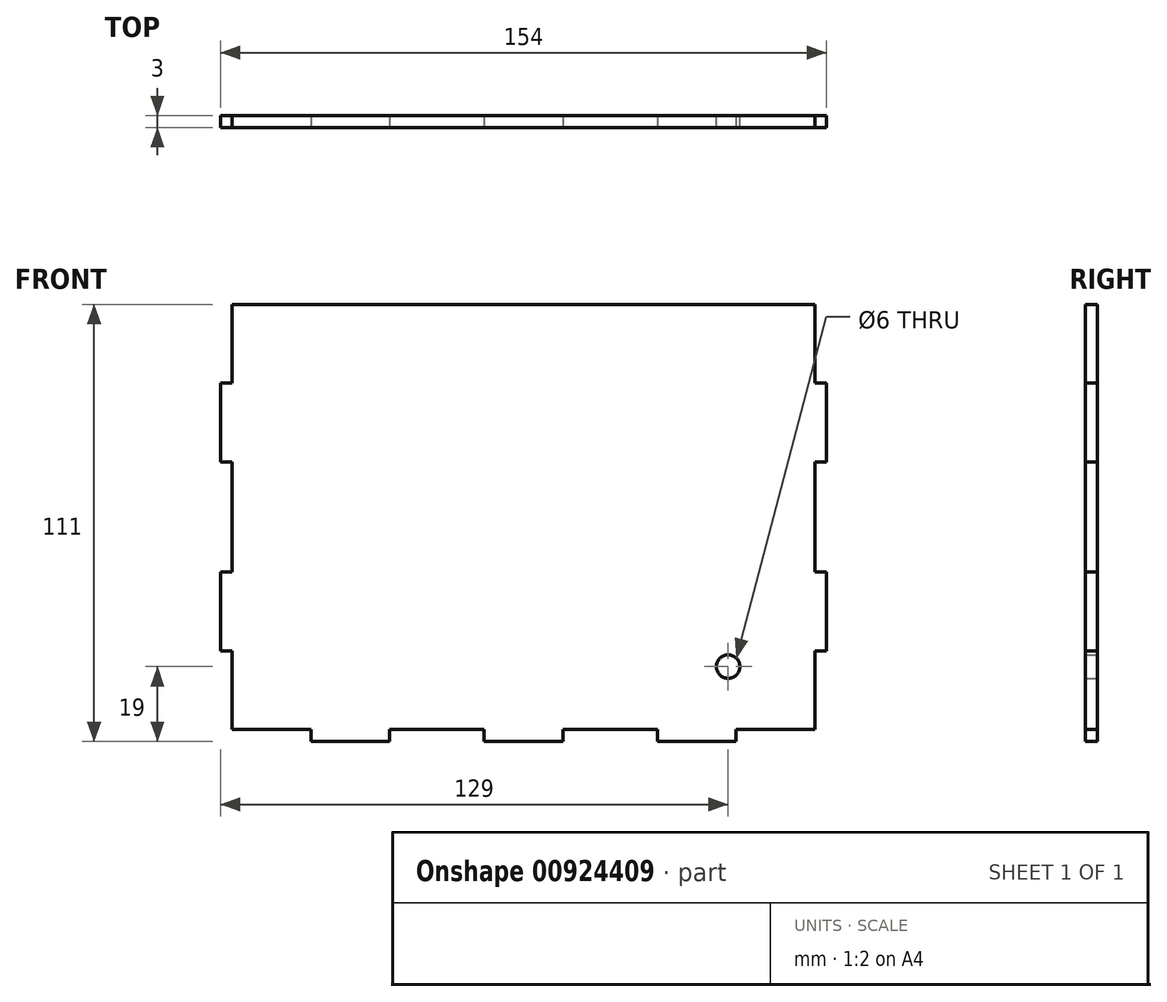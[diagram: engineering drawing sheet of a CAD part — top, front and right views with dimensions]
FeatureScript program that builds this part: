
annotation { "Feature Type Name" : "Feature", "Feature Type Description" : "" }
export const myFeature = defineFeature(function(context is Context, id is Id, definition is map)
    precondition{}
    {
        {
            var Q0;
            Q0=qCreatedBy(makeId("Front.planeOp"),FACE);
            var sketch = newSketch(context, id + "F0", { "sketchPlane" : qUnion([Q0])});
            skLineSegment(sketch, "E0.bottom", {"start": v(3, 0) * mm, "end": v(151, 0) * mm});
            skLineSegment(sketch, "E0.top", {"start": v(0, 111) * mm, "end": v(154, 111) * mm});
            skLineSegment(sketch, "E0.left", {"start": v(0, 3) * mm, "end": v(0, 111) * mm});
            skLineSegment(sketch, "E0.right", {"start": v(154, 3) * mm, "end": v(154, 111) * mm});
            skLineSegment(sketch, "E1", {"start": v(0, 3) * mm, "end": v(3, 3) * mm});
            skLineSegment(sketch, "E2", {"start": v(3, 3) * mm, "end": v(3, 0) * mm});
            skPoint(sketch, "E3", {"position": v(0, 55.5) * mm});
            skPoint(sketch, "E4.orphan", {"position": v(0, 0) * mm});
            skLineSegment(sketch, "E5", {"start": v(154, 3) * mm, "end": v(151, 3) * mm});
            skLineSegment(sketch, "E6", {"start": v(151, 3) * mm, "end": v(151, 0) * mm});
            skSolve(sketch);
        }
        {
            var Q0;
            Q0=qSketchRegion(id+"F0",true);
            extrude(context, id + "F1", {"entities" : qUnion([Q0]), "depth" : 3 * mm, "offsetDistance" : 25 * mm});
        }
        {
            var Q0;
            Q0=makeQuery(id+"F1.opExtrude","CAP_FACE",FACE,{"disambiguationData":[OSD([sQuery(id+"F0.wireOp",EDGE,"E0.bottom"),sQuery(id+"F0.wireOp",EDGE,"E0.top"),sQuery(id+"F0.wireOp",EDGE,"E0.left"),sQuery(id+"F0.wireOp",EDGE,"E0.right"),sQuery(id+"F0.wireOp",EDGE,"RRufsfr7-IhYP-SNug-Ydv5-wJAnrK0FF9g5"),sQuery(id+"F0.wireOp",EDGE,"Sx6Tzd0k-msLp-xlgR-asDp-E0VjmEOWkIfD"),sQuery(id+"F0.wireOp",EDGE,"E1"),sQuery(id+"F0.wireOp",EDGE,"E2"),sQuery(id+"F0.wireOp",EDGE,"xNTWjz4d-b93f-Mlsb-ypie-dKrJAlS9JbEo"),sQuery(id+"F0.wireOp",EDGE,"DDgqVk6M-NDhz-67C2-usiq-S1RQ2gWw5CQe"),sQuery(id+"F0.wireOp",EDGE,"E5"),sQuery(id+"F0.wireOp",EDGE,"E6")])],"isStart":false});
            var sketch = newSketch(context, id + "F2", { "sketchPlane" : qUnion([Q0])});
            skLineSegment(sketch, "E7.bottom", {"start": v(3, 0) * mm, "end": v(23, 0) * mm});
            skLineSegment(sketch, "E7.top", {"start": v(3, 3) * mm, "end": v(23, 3) * mm});
            skLineSegment(sketch, "E7.left", {"start": v(3, 0) * mm, "end": v(3, 3) * mm});
            skLineSegment(sketch, "E7.right", {"start": v(23, 0) * mm, "end": v(23, 3) * mm});
            skLineSegment(sketch, "E8.bottom", {"start": v(43, 0) * mm, "end": v(67, 0) * mm});
            skLineSegment(sketch, "E8.top", {"start": v(43, 3) * mm, "end": v(67, 3) * mm});
            skLineSegment(sketch, "E8.left", {"start": v(43, 0) * mm, "end": v(43, 3) * mm});
            skLineSegment(sketch, "E8.right", {"start": v(67, 0) * mm, "end": v(67, 3) * mm});
            skLineSegment(sketch, "E9.bottom", {"start": v(131, 0) * mm, "end": v(151, 0) * mm});
            skLineSegment(sketch, "E9.top", {"start": v(131, 3) * mm, "end": v(151, 3) * mm});
            skLineSegment(sketch, "E9.left", {"start": v(131, 0) * mm, "end": v(131, 3) * mm});
            skLineSegment(sketch, "E9.right", {"start": v(151, 0) * mm, "end": v(151, 3) * mm});
            skLineSegment(sketch, "E10", {"start": v(23, 1.5) * mm, "end": v(43, 1.5) * mm, "construction": true});
            skLineSegment(sketch, "E11", {"start": v(67, 1.5) * mm, "end": v(87, 1.5) * mm, "construction": true});
            skLineSegment(sketch, "E12.bottom", {"start": v(87, 0) * mm, "end": v(111, 0) * mm});
            skLineSegment(sketch, "E12.top", {"start": v(87, 3) * mm, "end": v(111, 3) * mm});
            skLineSegment(sketch, "E12.left", {"start": v(87, 0) * mm, "end": v(87, 3) * mm});
            skLineSegment(sketch, "E12.right", {"start": v(111, 0) * mm, "end": v(111, 3) * mm});
            skLineSegment(sketch, "E13", {"start": v(111, 1.5) * mm, "end": v(131, 1.5) * mm, "construction": true});
            skSolve(sketch);
        }
        {
            var Q0;
            Q0 = qSketchRegion(id + "F2", true);
            extrude(context, id + "F3", {"entities" : qUnion([Q0]), "operationType" : NewBodyOperationType.REMOVE, "endBound" : BoundingType.THROUGH_ALL, "oppositeDirection" : true, "depth" : 25 * mm, "offsetDistance" : 25 * mm});
        }
        {
            var Q0;
            Q0=makeQuery(id+"F1.opExtrude","CAP_FACE",FACE,{"disambiguationData":[OSD([sQuery(id+"F0.wireOp",EDGE,"E0.bottom"),sQuery(id+"F0.wireOp",EDGE,"E0.top"),sQuery(id+"F0.wireOp",EDGE,"E0.left"),sQuery(id+"F0.wireOp",EDGE,"E0.right"),sQuery(id+"F0.wireOp",EDGE,"E1"),sQuery(id+"F0.wireOp",EDGE,"E2"),sQuery(id+"F0.wireOp",EDGE,"E5"),sQuery(id+"F0.wireOp",EDGE,"E6")])],"isStart":true});
            var sketch = newSketch(context, id + "F4", { "sketchPlane" : qUnion([Q0])});
            skLineSegment(sketch, "E14.bottom", {"start": v(-154, 3) * mm, "end": v(-151, 3) * mm});
            skLineSegment(sketch, "E14.top", {"start": v(-154, 23) * mm, "end": v(-151, 23) * mm});
            skLineSegment(sketch, "E14.left", {"start": v(-154, 3) * mm, "end": v(-154, 23) * mm});
            skLineSegment(sketch, "E14.right", {"start": v(-151, 3) * mm, "end": v(-151, 23) * mm});
            skLineSegment(sketch, "E15.bottom", {"start": v(-154, 43) * mm, "end": v(-151, 43) * mm});
            skLineSegment(sketch, "E15.top", {"start": v(-154, 71) * mm, "end": v(-151, 71) * mm});
            skLineSegment(sketch, "E15.left", {"start": v(-154, 43) * mm, "end": v(-154, 71) * mm});
            skLineSegment(sketch, "E15.right", {"start": v(-151, 43) * mm, "end": v(-151, 71) * mm});
            skLineSegment(sketch, "E16.bottom", {"start": v(-154, 91) * mm, "end": v(-151, 91) * mm});
            skLineSegment(sketch, "E16.top", {"start": v(-154, 111) * mm, "end": v(-151, 111) * mm});
            skLineSegment(sketch, "E16.left", {"start": v(-154, 91) * mm, "end": v(-154, 111) * mm});
            skLineSegment(sketch, "E16.right", {"start": v(-151, 91) * mm, "end": v(-151, 111) * mm});
            skLineSegment(sketch, "E17", {"start": v(-77, 0) * mm, "end": v(-77, 111) * mm, "construction": true});
            skLineSegment(sketch, "E18.MirrorCS", {"start": v(0, 43) * mm, "end": v(-3, 43) * mm});
            skLineSegment(sketch, "E19.MirrorCS", {"start": v(0, 71) * mm, "end": v(-3, 71) * mm});
            skLineSegment(sketch, "E20.MirrorCS", {"start": v(0, 23) * mm, "end": v(-3, 23) * mm});
            skLineSegment(sketch, "E21.MirrorCS", {"start": v(0, 111) * mm, "end": v(-3, 111) * mm});
            skLineSegment(sketch, "E22.MirrorCS", {"start": v(0, 91) * mm, "end": v(-3, 91) * mm});
            skLineSegment(sketch, "E23.MirrorCS", {"start": v(0, 3) * mm, "end": v(-3, 3) * mm});
            skLineSegment(sketch, "E24.MirrorCS", {"start": v(-3, 3) * mm, "end": v(-3, 23) * mm});
            skLineSegment(sketch, "E25.MirrorCS", {"start": v(0, 43) * mm, "end": v(0, 71) * mm});
            skLineSegment(sketch, "E26.MirrorCS", {"start": v(-3, 43) * mm, "end": v(-3, 71) * mm});
            skLineSegment(sketch, "E27.MirrorCS", {"start": v(-3, 91) * mm, "end": v(-3, 111) * mm});
            skLineSegment(sketch, "E28.MirrorCS", {"start": v(0, 3) * mm, "end": v(0, 23) * mm});
            skLineSegment(sketch, "E29.MirrorCS", {"start": v(0, 91) * mm, "end": v(0, 111) * mm});
            skSolve(sketch);
        }
        {
            var Q0;
            Q0 = qSketchRegion(id + "F4", true);
            extrude(context, id + "F5", {"entities" : qUnion([Q0]), "operationType" : NewBodyOperationType.REMOVE, "endBound" : BoundingType.THROUGH_ALL, "oppositeDirection" : true, "depth" : 25 * mm, "offsetDistance" : 25 * mm});
        }
        {
            var Q0;
            Q0=makeQuery(id+"F1.opExtrude","CAP_FACE",FACE,{"disambiguationData":[OSD([sQuery(id+"F0.wireOp",EDGE,"E0.bottom"),sQuery(id+"F0.wireOp",EDGE,"E0.top"),sQuery(id+"F0.wireOp",EDGE,"E0.left"),sQuery(id+"F0.wireOp",EDGE,"E0.right"),sQuery(id+"F0.wireOp",EDGE,"E1"),sQuery(id+"F0.wireOp",EDGE,"E2"),sQuery(id+"F0.wireOp",EDGE,"E5"),sQuery(id+"F0.wireOp",EDGE,"E6")])],"isStart":true});
            var sketch = newSketch(context, id + "F6", { "sketchPlane" : qUnion([Q0])});
            skCircle(sketch, "E30", {"center": v(-129, 19) * mm, "radius": 3 * mm});
            skSolve(sketch);
        }
        {
            var Q0;
            Q0 = qSketchRegion(id + "F6", true);
            extrude(context, id + "F7", {"entities" : qUnion([Q0]), "operationType" : NewBodyOperationType.REMOVE, "endBound" : BoundingType.THROUGH_ALL, "oppositeDirection" : true, "depth" : 25 * mm, "offsetDistance" : 25 * mm});
        }
    });
